# Revit family: Langley round vessel - BIM REVIT - Copy
name_source: partatom
category: Plumbing Fixtures
revit_build: Autodesk Revit 2015 (Build: 20140606_1530(x64)
units: mm (PartAtom-declared; Revit-internal decimal feet)

## types (1)
- LANGLEY ROUND VESSEL BASIN, NO TH
    BIMobject category = Basins
    BIMobject category code = sanitary-basins
    BIMobject main category = Sanitary
    BIMobject main category code = sanitary
    BOSUseNativeGeometries = 1
    Brand url = www.theswc.co.uk
    Date of publishing = 1/6/2019
    Default Elevation = 4' - 0"
    Description = Langley round countertop mounted vessel vanity basin, no tap hole or overflow
    Edition number = 1
    IFC Classification = Sanitary Terminal
    MEP Diameter = 3"
    Manufacturer = The Sanitaryware Company
    Manufacturer country = United Arab Emirates
    Manufacturer name = The Sanitaryware Company
    Material main = Ceramics
    Material secondary = Ceramics
    Model = LLWB122
    NBS Reference Code = 31-79
    NBS Reference Description = Sinks, Wash Basins And Troughs
    Nominal height = 0' - 5 1/8"
    Nominal width = 1' - 4 17/32"
    Product SKU = Langley Round Vessel Basin, NO TH, LLWB122
    Product certification = www.theswc.co.uk
    Product family = Langley
    Product group = Basins
    Uniclass 1.4 Code = L7212
    Uniclass 1.4 Description = Washbasins
    Uniclass 2.0 Code = PR-31-79
    Uniclass 2.0 Description = Sinks, Wash Basins And Troughs
    Uniclass 2015 Code = Pr_40_20_96
    Uniclass 2015 Name = Wash basins, sinks and troughs
    Weight Net (Kg) = 9

## geometry (parser evidence)
native form markers: Sweep x3
no freeform markers — native parametric forms only
